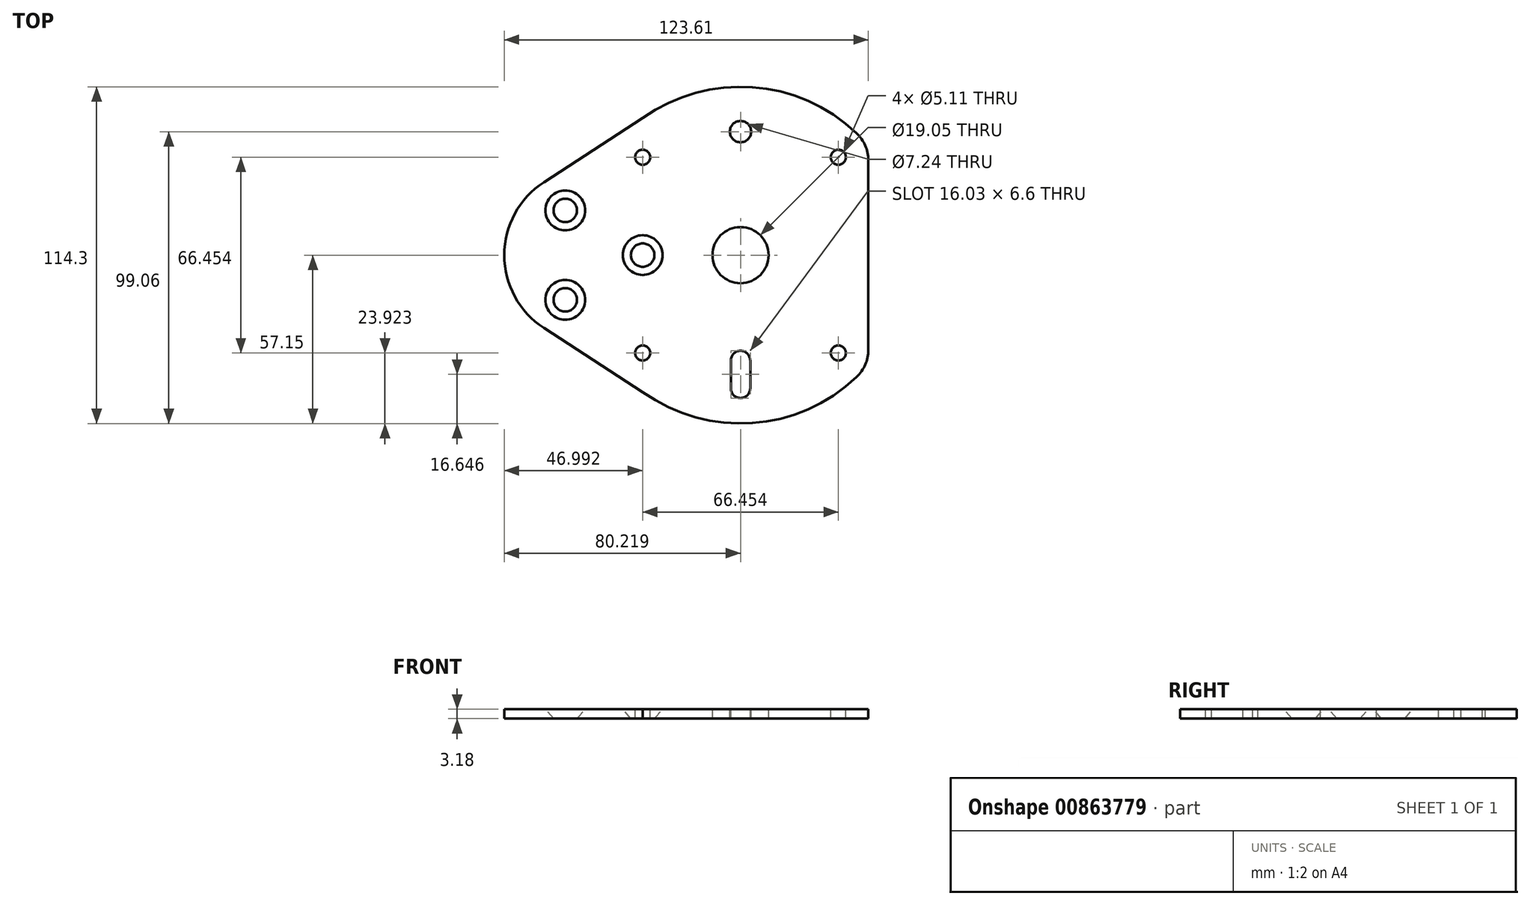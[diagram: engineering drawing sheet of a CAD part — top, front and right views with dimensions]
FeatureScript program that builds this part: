
annotation { "Feature Type Name" : "Feature", "Feature Type Description" : "" }
export const myFeature = defineFeature(function(context is Context, id is Id, definition is map)
    precondition{}
    {
        {
            var Q0;
            Q0=qCreatedBy(makeId("Top.planeOp"),FACE);
            var sketch = newSketch(context, id + "F0", { "sketchPlane" : qUnion([Q0])});
            skLineSegment(sketch, "E0", {"start": v(0, 0) * mm, "end": v(-58.93, 0) * mm, "construction": true});
            skPoint(sketch, "E1", {"position": v(-29.46, 0) * mm});
            skCircle(sketch, "E2", {"center": v(-29.46, 0) * mm, "radius": 17.53 * mm, "construction": true});
            skPoint(sketch, "E3", {"position": v(21.29, 0) * mm});
            skPoint(sketch, "E4", {"position": v(-11.94, 0) * mm});
            skCircle(sketch, "E5", {"center": v(21.29, 0) * mm, "radius": 19.05 * mm, "construction": true});
            skCircle(sketch, "E6", {"center": v(21.29, 0) * mm, "radius": 31.75 * mm, "construction": true});
            skCircle(sketch, "E7", {"center": v(54.52, 33.23) * mm, "radius": 2.55 * mm});
            skCircle(sketch, "E8", {"center": v(21.29, 0) * mm, "radius": 9.53 * mm});
            skCircle(sketch, "E9", {"center": v(21.29, 0) * mm, "radius": 35.94 * mm, "construction": true});
            skLineSegment(sketch, "E10", {"start": v(21.29, 57.15) * mm, "end": v(21.29, -57.15) * mm, "construction": true});
            skCircle(sketch, "E11", {"center": v(21.29, 0) * mm, "radius": 45.34 * mm, "construction": true});
            skLineSegment(sketch, "E12", {"start": v(21.29, 0) * mm, "end": v(61.7, 40.41) * mm, "construction": true});
            skCircle(sketch, "E13", {"center": v(21.29, 0) * mm, "radius": 46.99 * mm, "construction": true});
            skCircle(sketch, "E14.1.0", {"center": v(-11.94, 33.23) * mm, "radius": 2.55 * mm});
            skCircle(sketch, "E14.2.0", {"center": v(-11.94, -33.23) * mm, "radius": 2.55 * mm});
            skCircle(sketch, "E14.3.0", {"center": v(54.52, -33.23) * mm, "radius": 2.55 * mm});
            skLineSegment(sketch, "E15", {"start": v(21.29, 0) * mm, "end": v(-19.12, 40.41) * mm, "construction": true});
            skLineSegment(sketch, "E16", {"start": v(21.29, 0) * mm, "end": v(-19.12, -40.41) * mm, "construction": true});
            skCircle(sketch, "E17", {"center": v(21.29, 0) * mm, "radius": 57.15 * mm, "construction": true});
            skCircle(sketch, "E18.converted", {"center": v(-29.46, 0) * mm, "radius": 29.46 * mm, "construction": true});
            skPoint(sketch, "E19", {"position": v(78.44, 0) * mm});
            skLineSegment(sketch, "E20", {"start": v(-38.23, 28.13) * mm, "end": v(-38.23, -28.13) * mm, "construction": true});
            skLineSegment(sketch, "E21", {"start": v(-11.94, -46.5) * mm, "end": v(-11.94, 46.5) * mm, "construction": true});
            skLineSegment(sketch, "E22", {"start": v(17.99, -35.79) * mm, "end": v(17.99, -45.22) * mm});
            skLineSegment(sketch, "E23", {"start": v(24.6, -35.79) * mm, "end": v(24.6, -45.22) * mm});
            skArc(sketch, "E24", {"start": v(17.99, -35.79) * mm, "mid": v(21.29, -32.49) * mm, "end": v(24.6, -35.79) * mm});
            skArc(sketch, "E25", {"start": v(17.99, -45.22) * mm, "mid": v(21.29, -48.52) * mm, "end": v(24.6, -45.22) * mm});
            skLineSegment(sketch, "E26", {"start": v(64.68, 32.16) * mm, "end": v(64.68, -18.05) * mm});
            skArc(sketch, "E27", {"start": v(60.74, 41.35) * mm, "mid": v(25.33, 57) * mm, "end": v(-11.94, 46.5) * mm});
            skArc(sketch, "E28", {"start": v(-11.94, -46.5) * mm, "mid": v(25.33, -57) * mm, "end": v(60.74, -41.35) * mm});
            skPoint(sketch, "E29.visualSharp", {"position": v(64.68, 37.2) * mm});
            skArc(sketch, "E29.filletArc", {"start": v(64.68, 32.16) * mm, "mid": v(63.65, 37.15) * mm, "end": v(60.74, 41.35) * mm});
            skPoint(sketch, "E30.visualSharp", {"position": v(64.68, -37.2) * mm});
            skArc(sketch, "E30.filletArc", {"start": v(60.74, -41.35) * mm, "mid": v(63.65, -37.15) * mm, "end": v(64.68, -32.16) * mm});
            skPoint(sketch, "E31.visualSharp", {"position": v(-38.23, 28.13) * mm});
            skPoint(sketch, "E32.visualSharp", {"position": v(-38.23, -28.13) * mm});
            skLineSegment(sketch, "E33.trimOffspring", {"start": v(64.68, -18.05) * mm, "end": v(64.68, -32.16) * mm});
            skLineSegment(sketch, "E34", {"start": v(-11.94, 46.5) * mm, "end": v(-45.5, 24.72) * mm});
            skLineSegment(sketch, "E35", {"start": v(-11.94, -46.5) * mm, "end": v(-45.5, -24.72) * mm});
            skArc(sketch, "E36", {"start": v(-45.5, 24.72) * mm, "mid": v(-58.93, 0) * mm, "end": v(-45.5, -24.72) * mm});
            skCircle(sketch, "E37", {"center": v(21.29, 41.91) * mm, "radius": 3.62 * mm});
            skPoint(sketch, "E38", {"position": v(-38.23, 15.18) * mm});
            skPoint(sketch, "E39", {"position": v(-38.23, -15.18) * mm});
            skSolve(sketch);
        }
        {
            var Q0;
            Q0=makeQuery(id+"F0.imprint","IMPRINT",FACE,{"disambiguationData":[TD([[makeQuery(id+"F0.imprint","IMPRINT",EDGE,{"derivedFrom":sQuery(id+"F0.wireOp",EDGE,"E7")}),-1.0]])]});
            extrude(context, id + "F1", {"entities" : qUnion([Q0]), "oppositeDirection" : true, "depth" : 3.17 * mm, "offsetDistance" : 25.4 * mm});
        }
        {
            var Q0;
            Q0=sQuery(id+"F0.wireOp",VERTEX,"E38");
            var Q1;
            Q1=sQuery(id+"F0.wireOp",VERTEX,"E4");
            var Q2;
            Q2=sQuery(id+"F0.wireOp",VERTEX,"E39");
            var Q3;
            Q3=makeQuery(id+"F1.opExtrude","SWEPT_BODY",BODY,{"disambiguationData":[OSD([sQuery(id+"F0.wireOp",EDGE,"E7"),sQuery(id+"F0.wireOp",EDGE,"E8"),sQuery(id+"F0.wireOp",EDGE,"E14.1.0"),sQuery(id+"F0.wireOp",EDGE,"E14.2.0"),sQuery(id+"F0.wireOp",EDGE,"E14.3.0"),sQuery(id+"F0.wireOp",EDGE,"E22"),sQuery(id+"F0.wireOp",EDGE,"E23"),sQuery(id+"F0.wireOp",EDGE,"E24"),sQuery(id+"F0.wireOp",EDGE,"E25"),sQuery(id+"F0.wireOp",EDGE,"E26"),sQuery(id+"F0.wireOp",EDGE,"E27"),sQuery(id+"F0.wireOp",EDGE,"E28"),sQuery(id+"F0.wireOp",EDGE,"E29.filletArc"),sQuery(id+"F0.wireOp",EDGE,"E30.filletArc"),sQuery(id+"F0.wireOp",EDGE,"E33.trimOffspring"),sQuery(id+"F0.wireOp",EDGE,"E34"),sQuery(id+"F0.wireOp",EDGE,"E35"),sQuery(id+"F0.wireOp",EDGE,"E36"),sQuery(id+"F0.wireOp",EDGE,"E37")])]});
            hole(context, id + "F2", {"style" : HoleStyle.C_SINK, "endStyle" : HoleEndStyle.THROUGH, "standardTappedOrClearance" : lookupTablePath({ "fit" : "Normal (ASME)", "standard" : "ANSI", "size" : "1/4", "type" : "Clearance" }), "standardBlindInLast" : lookupTablePath({ "fit" : "Normal", "standard" : "ANSI", "engagement" : "75%", "pitch" : "20 tpi", "size" : "1/4", "type" : "Clearance & tapped" }), "holeDiameter" : 7.14 * mm, "cSinkDiameter" : 13.5 * mm, "cSinkAngle" : 82 * degree, "majorDiameter" : 6.35 * mm, "isTappedThrough" : true, "tappedDepth" : 12.7 * mm, "tapClearance" : 3, "locations" : qUnion([Q0, Q1, Q2]), "scope" : qUnion([Q3])});
        }
    });
